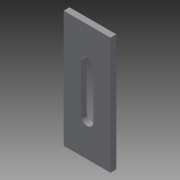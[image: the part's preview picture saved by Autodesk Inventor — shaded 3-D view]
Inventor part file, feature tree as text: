
AUTODESK INVENTOR PART (.ipt)
format: ipt  version: 2013 (Build 170138000, 138)  size: 82,432 bytes
history: native  units: in
note: dims shown in document units (in); Inventor stores cm internally (conversion verified against a paired STEP export)
features: sheet_metal_op x1, sketch x1, other x1
ambient origin geometry x8: Origin, YZ Plane, XZ Plane, XY Plane, X Axis, Y Axis, Z Axis, Center Point
bodies: Solid1 (feature_tree)
feature tree (3):
  sheet_metal_op  "Face1"
  sketch  "Sketch1"  dims[d0=1.0in d1=0.125in]
  other  "Plate1"
